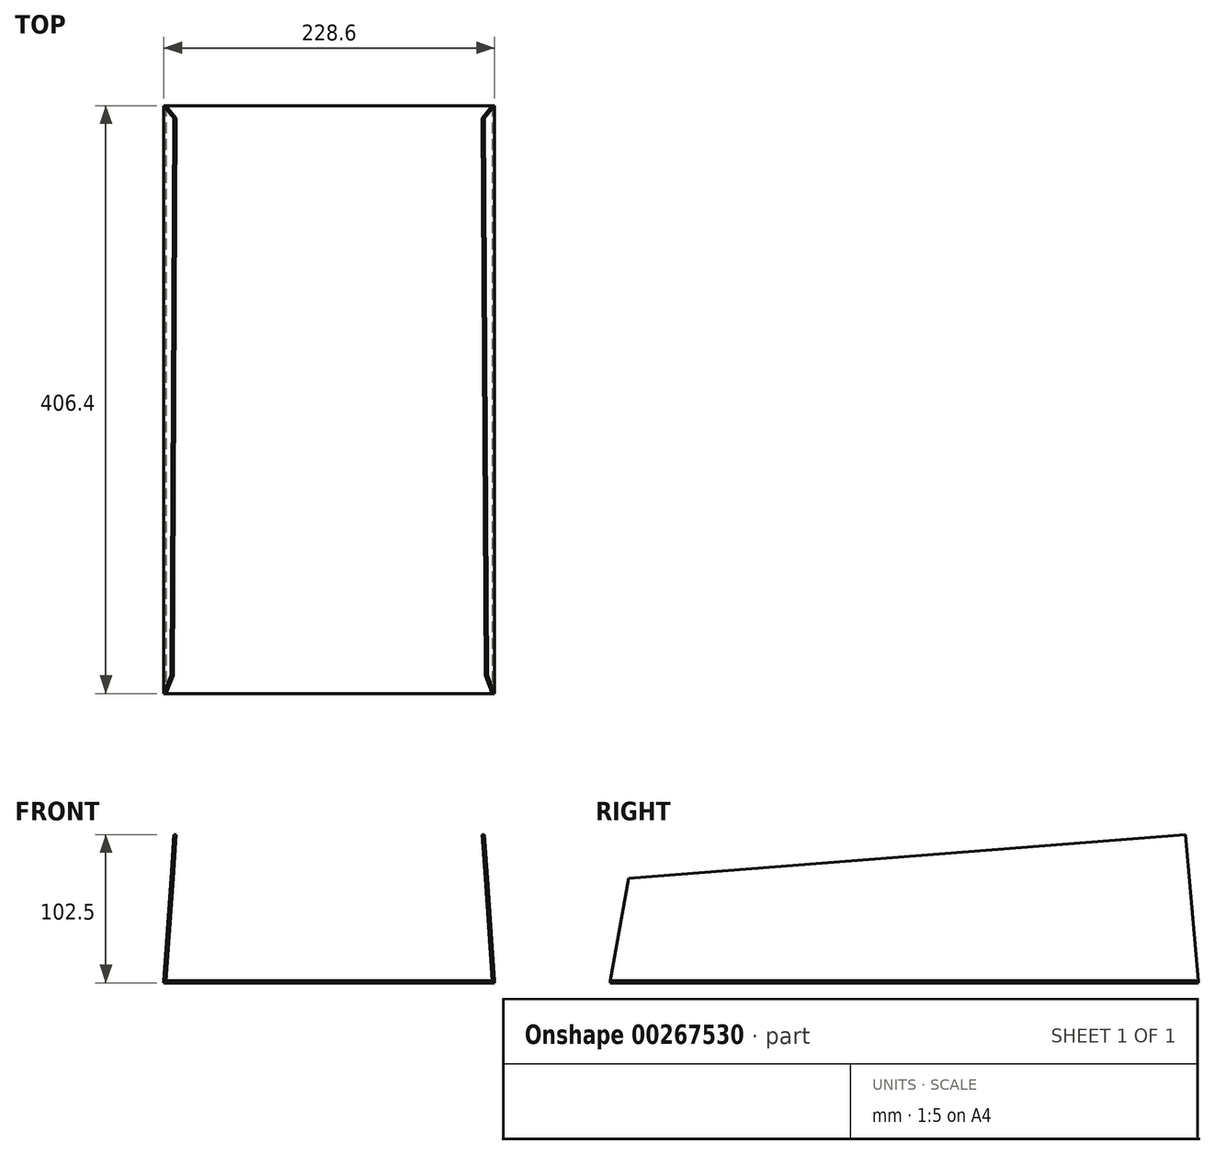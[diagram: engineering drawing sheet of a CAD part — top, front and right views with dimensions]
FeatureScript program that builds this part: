
annotation { "Feature Type Name" : "Feature", "Feature Type Description" : "" }
export const myFeature = defineFeature(function(context is Context, id is Id, definition is map)
    precondition{}
    {
        {
            var Q0;
            Q0=qCreatedBy(makeId("Top.planeOp"),FACE);
            var sketch = newSketch(context, id + "F0", { "sketchPlane" : qUnion([Q0])});
            skLineSegment(sketch, "E0.bottom", {"start": v(-114.3, 203.2) * mm, "end": v(114.3, 203.2) * mm});
            skLineSegment(sketch, "E0.top", {"start": v(-114.3, -203.2) * mm, "end": v(114.3, -203.2) * mm});
            skLineSegment(sketch, "E0.left", {"start": v(-114.3, 203.2) * mm, "end": v(-114.3, -203.2) * mm});
            skLineSegment(sketch, "E0.right", {"start": v(114.3, 203.2) * mm, "end": v(114.3, -203.2) * mm});
            skPoint(sketch, "E0.middle", {"position": v(0, 0) * mm});
            skSolve(sketch);
        }
        {
            var Q0;
            Q0=makeQuery(id+"F0.imprint","IMPRINT",FACE,{"disambiguationData":[TD([[makeQuery(id+"F0.imprint","IMPRINT",EDGE,{"derivedFrom":sQuery(id+"F0.wireOp",EDGE,"E0.bottom")}),-1.0]])]});
            extrude(context, id + "F1", {"entities" : qUnion([Q0]), "depth" : 1.59 * mm});
        }
        {
            var Q0;
            Q0=makeQuery(id+"F1.opExtrude","SWEPT_FACE",FACE,{"disambiguationData":[OSD([sQuery(id+"F0.wireOp",EDGE,"E0.bottom")])]});
            var sketch = newSketch(context, id + "F2", { "sketchPlane" : qUnion([Q0])});
            skLineSegment(sketch, "E1", {"start": v(114.3, 1.59) * mm, "end": v(107.2, 103.19) * mm});
            skLineSegment(sketch, "E2", {"start": v(107.2, 103.19) * mm, "end": v(105.61, 103.08) * mm});
            skLineSegment(sketch, "E3", {"start": v(105.61, 103.08) * mm, "end": v(112.7, 1.59) * mm});
            skLineSegment(sketch, "E4", {"start": v(112.7, 1.59) * mm, "end": v(114.3, 1.59) * mm});
            skSolve(sketch);
        }
        {
            var Q0;
            Q0=makeQuery(id+"F1.opExtrude","SWEPT_FACE",FACE,{"disambiguationData":[OSD([sQuery(id+"F0.wireOp",EDGE,"E0.top")])]});
            var sketch = newSketch(context, id + "F3", { "sketchPlane" : qUnion([Q0])});
            skLineSegment(sketch, "E5", {"start": v(-114.3, 1.59) * mm, "end": v(-109.42, 71.44) * mm});
            skLineSegment(sketch, "E6", {"start": v(-109.42, 71.44) * mm, "end": v(-107.83, 71.33) * mm});
            skLineSegment(sketch, "E7", {"start": v(-107.83, 71.33) * mm, "end": v(-112.7, 1.59) * mm});
            skLineSegment(sketch, "E8", {"start": v(-112.7, 1.59) * mm, "end": v(-114.3, 1.59) * mm});
            skSolve(sketch);
        }
        {
            var Q1;
            Q1=makeQuery(id+"F2.imprint","IMPRINT",FACE,{"disambiguationData":[TD([[makeQuery(id+"F2.imprint","IMPRINT",EDGE,{"derivedFrom":sQuery(id+"F2.wireOp",EDGE,"E1")}),1.0]])]});
            var Q2;
            Q2=makeQuery(id+"F3.imprint","IMPRINT",FACE,{"disambiguationData":[TD([[makeQuery(id+"F3.imprint","IMPRINT",EDGE,{"derivedFrom":sQuery(id+"F3.wireOp",EDGE,"E5")}),-1.0]])]});
            loft(context, id + "F4", {"sheetProfilesArray" : [{ "sheetProfileEntities" : qUnion([Q1]) }, { "sheetProfileEntities" : qUnion([Q2]) }]});
        }
        {
            var Q0;
            Q0=qCreatedBy(makeId("Right.planeOp"),FACE);
            var sketch = newSketch(context, id + "F5", { "sketchPlane" : qUnion([Q0])});
            skLineSegment(sketch, "E9", {"start": v(203.2, 1.59) * mm, "end": v(192.94, 118.8) * mm});
            skLineSegment(sketch, "E10", {"start": v(192.94, 118.8) * mm, "end": v(203.2, 118.8) * mm});
            skLineSegment(sketch, "E11", {"start": v(203.2, 118.8) * mm, "end": v(203.2, 1.59) * mm});
            skLineSegment(sketch, "E12", {"start": v(-203.2, 1.59) * mm, "end": v(-203.2, 88.57) * mm});
            skLineSegment(sketch, "E13", {"start": v(-203.2, 88.57) * mm, "end": v(-187.86, 88.57) * mm});
            skLineSegment(sketch, "E14", {"start": v(-187.86, 88.57) * mm, "end": v(-203.2, 1.59) * mm});
            skSolve(sketch);
        }
        {
            var Q0;
            Q0=makeQuery(id+"F4.opLoft","SWEPT_BODY",BODY,{"disambiguationData":[OSD([makeQuery(id+"F2.imprint","IMPRINT",FACE,{"disambiguationData":[TD([[makeQuery(id+"F2.imprint","IMPRINT",EDGE,{"derivedFrom":sQuery(id+"F2.wireOp",EDGE,"E1")}),1.0]])]}),makeQuery(id+"F3.imprint","IMPRINT",FACE,{"disambiguationData":[TD([[makeQuery(id+"F3.imprint","IMPRINT",EDGE,{"derivedFrom":sQuery(id+"F3.wireOp",EDGE,"E5")}),-1.0]])]})])]});
            var Q1;
            Q1=qCreatedBy(makeId("Right.planeOp"),FACE);
            mirror(context, id + "F6", {"entities" : qUnion([Q0]), "mirrorPlane" : qUnion([Q1])});
        }
        {
            var Q0;
            Q0=makeQuery(id+"F5.imprint","IMPRINT",FACE,{"disambiguationData":[TD([[makeQuery(id+"F5.imprint","IMPRINT",EDGE,{"derivedFrom":sQuery(id+"F5.wireOp",EDGE,"E9")}),-1.0]])]});
            var Q1;
            Q1=makeQuery(id+"F5.imprint","IMPRINT",FACE,{"disambiguationData":[TD([[makeQuery(id+"F5.imprint","IMPRINT",EDGE,{"derivedFrom":sQuery(id+"F5.wireOp",EDGE,"E12")}),-1.0]])]});
            extrude(context, id + "F7", {"entities" : qUnion([Q0, Q1]), "operationType" : NewBodyOperationType.REMOVE, "oppositeDirection" : true, "depth" : 203.2 * mm, "hasSecondDirection" : true, "secondDirectionOppositeDirection" : false, "secondDirectionDepth" : 147.32 * mm});
        }
        {
            var Q0;
            Q0=qCreatedBy(makeId("Front.planeOp"),FACE);
            cPlane(context, id + "F8", {"entities" : qUnion([Q0]), "cplaneType" : CPlaneType.OFFSET, "offset" : 127 * mm, "width" : 152.4 * mm, "height" : 152.4 * mm});
        }
    });
